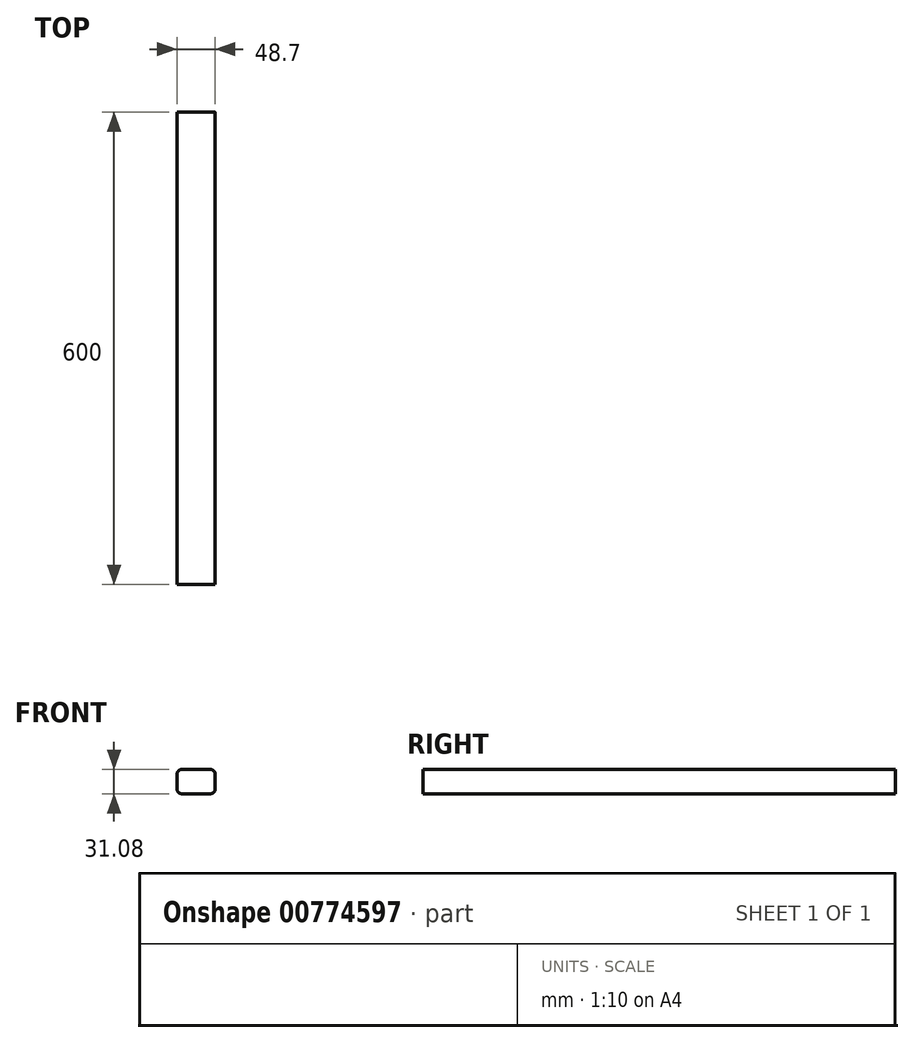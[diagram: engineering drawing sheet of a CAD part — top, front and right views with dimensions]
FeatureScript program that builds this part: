
annotation { "Feature Type Name" : "Feature", "Feature Type Description" : "" }
export const myFeature = defineFeature(function(context is Context, id is Id, definition is map)
    precondition{}
    {
        {
            var Q0;
            Q0=qCreatedBy(makeId("Front.planeOp"),FACE);
            var sketch = newSketch(context, id + "F0", { "sketchPlane" : qUnion([Q0])});
            skLineSegment(sketch, "E0.bottom", {"start": v(18, -15.54) * mm, "end": v(-18, -15.54) * mm});
            skLineSegment(sketch, "E0.top", {"start": v(18, 15.54) * mm, "end": v(-18, 15.54) * mm});
            skLineSegment(sketch, "E0.left", {"start": v(24.35, -9.19) * mm, "end": v(24.35, 9.19) * mm});
            skLineSegment(sketch, "E0.right", {"start": v(-24.35, -9.19) * mm, "end": v(-24.35, 9.19) * mm});
            skPoint(sketch, "E0.middle", {"position": v(0, 0) * mm});
            skPoint(sketch, "E1.visualSharp", {"position": v(-24.35, 15.54) * mm});
            skArc(sketch, "E1.filletArc", {"start": v(-18, 15.54) * mm, "mid": v(-22.49, 13.68) * mm, "end": v(-24.35, 9.19) * mm});
            skPoint(sketch, "E2.visualSharp", {"position": v(24.35, -15.54) * mm});
            skArc(sketch, "E2.filletArc", {"start": v(18, -15.54) * mm, "mid": v(22.49, -13.68) * mm, "end": v(24.35, -9.19) * mm});
            skPoint(sketch, "E3.visualSharp", {"position": v(24.35, 15.54) * mm});
            skArc(sketch, "E3.filletArc", {"start": v(24.35, 9.19) * mm, "mid": v(22.49, 13.68) * mm, "end": v(18, 15.54) * mm});
            skPoint(sketch, "E4.visualSharp", {"position": v(-24.35, -15.54) * mm});
            skArc(sketch, "E4.filletArc", {"start": v(-24.35, -9.19) * mm, "mid": v(-22.49, -13.68) * mm, "end": v(-18, -15.54) * mm});
            skSolve(sketch);
        }
        {
            var Q0;
            Q0=makeQuery(id+"F0.imprint","IMPRINT",FACE,{"disambiguationData":[TD([[makeQuery(id+"F0.imprint","IMPRINT",EDGE,{"derivedFrom":sQuery(id+"F0.wireOp",EDGE,"E0.bottom")}),-1.0]])]});
            extrude(context, id + "F1", {"entities" : qUnion([Q0]), "depth" : 600 * mm, "offsetDistance" : 25.4 * mm});
        }
    });
